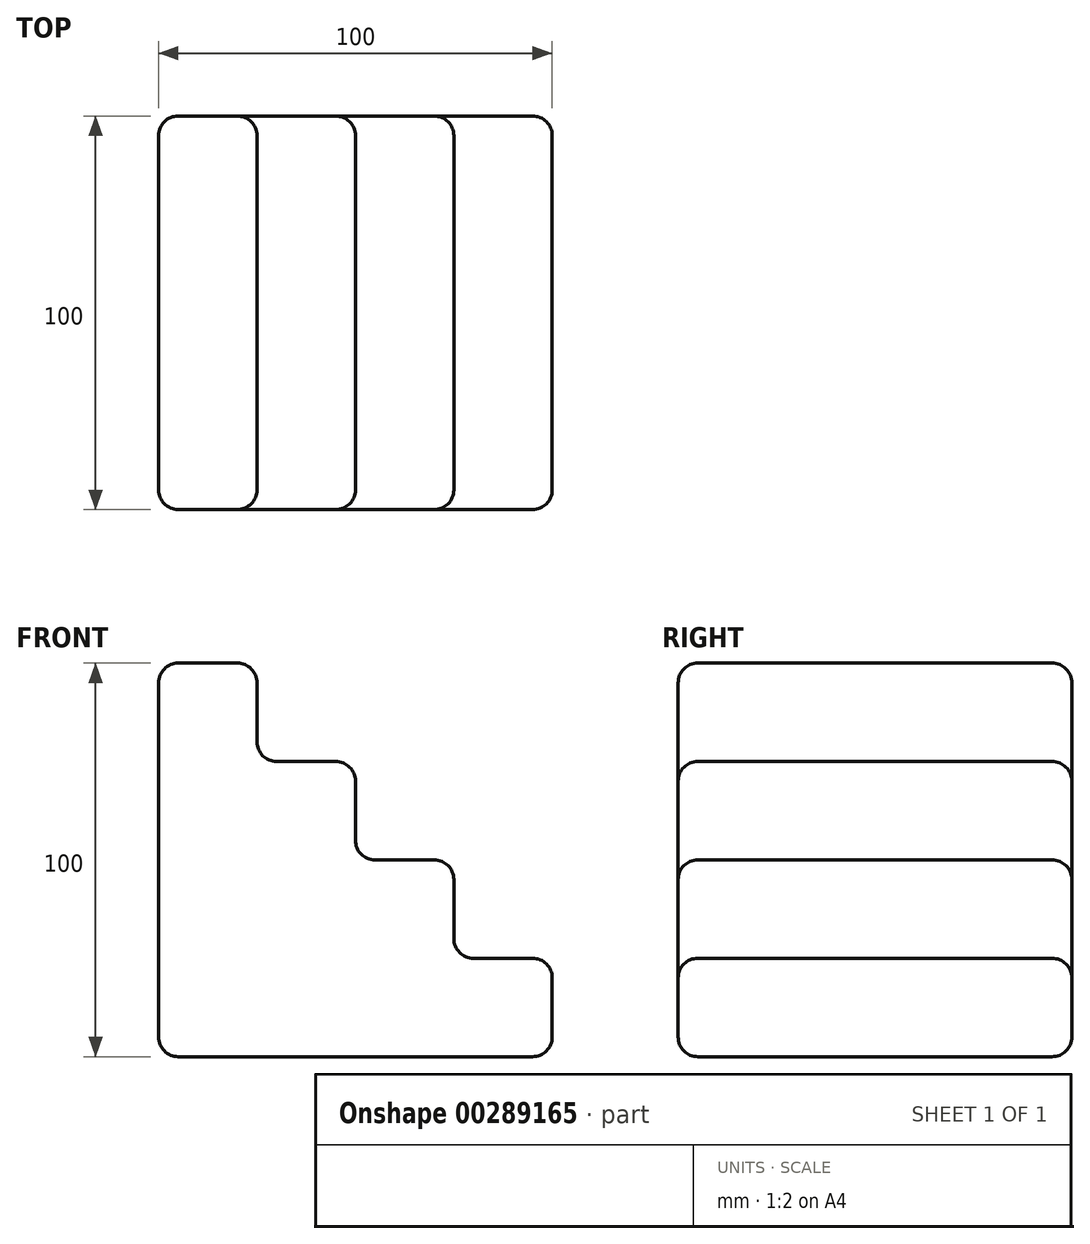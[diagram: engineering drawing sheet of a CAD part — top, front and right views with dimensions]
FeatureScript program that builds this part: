
annotation { "Feature Type Name" : "Feature", "Feature Type Description" : "" }
export const myFeature = defineFeature(function(context is Context, id is Id, definition is map)
    precondition{}
    {
        {
            var Q0;
            Q0=qCreatedBy(makeId("Front.planeOp"),FACE);
            var sketch = newSketch(context, id + "F0", { "sketchPlane" : qUnion([Q0])});
            skLineSegment(sketch, "E0.bottom", {"start": v(0, 0) * mm, "end": v(100, 0) * mm});
            skLineSegment(sketch, "E0.top", {"start": v(0, 100) * mm, "end": v(25, 100) * mm});
            skLineSegment(sketch, "E0.left", {"start": v(0, 0) * mm, "end": v(0, 100) * mm});
            skLineSegment(sketch, "E0.right", {"start": v(100, 0) * mm, "end": v(100, 25) * mm});
            skLineSegment(sketch, "E1", {"start": v(25, 100) * mm, "end": v(25, 75) * mm});
            skLineSegment(sketch, "E2", {"start": v(25, 75) * mm, "end": v(50, 75) * mm});
            skLineSegment(sketch, "E3", {"start": v(50, 75) * mm, "end": v(50, 50) * mm});
            skLineSegment(sketch, "E4", {"start": v(50, 50) * mm, "end": v(75, 50) * mm});
            skLineSegment(sketch, "E5", {"start": v(75, 50) * mm, "end": v(75, 25) * mm});
            skLineSegment(sketch, "E6", {"start": v(75, 25) * mm, "end": v(100, 25) * mm});
            skSolve(sketch);
        }
        {
            var Q0;
            Q0=makeQuery(id+"F0.imprint","IMPRINT",FACE,{"disambiguationData":[TD([[makeQuery(id+"F0.imprint","IMPRINT",EDGE,{"derivedFrom":sQuery(id+"F0.wireOp",EDGE,"E0.bottom")}),1.0]])]});
            extrude(context, id + "F1", {"entities" : qUnion([Q0]), "depth" : 100 * mm});
        }
        {
            var Q0;
            Q0=makeQuery(id+"F1.opExtrude","SWEPT_EDGE",EDGE,{"disambiguationData":[OSD([sQuery(id+"F0.wireOp",EDGE,"E0.top"),sQuery(id+"F0.wireOp",EDGE,"E1")])]});
            var Q1;
            Q1=makeQuery(id+"F1.opExtrude","SWEPT_EDGE",EDGE,{"disambiguationData":[OSD([sQuery(id+"F0.wireOp",EDGE,"E1"),sQuery(id+"F0.wireOp",EDGE,"E2")])]});
            var Q2;
            Q2=makeQuery(id+"F1.opExtrude","SWEPT_EDGE",EDGE,{"disambiguationData":[OSD([sQuery(id+"F0.wireOp",EDGE,"E2"),sQuery(id+"F0.wireOp",EDGE,"E3")])]});
            var Q3;
            Q3=makeQuery(id+"F1.opExtrude","SWEPT_EDGE",EDGE,{"disambiguationData":[OSD([sQuery(id+"F0.wireOp",EDGE,"E3"),sQuery(id+"F0.wireOp",EDGE,"E4")])]});
            var Q4;
            Q4=makeQuery(id+"F1.opExtrude","SWEPT_EDGE",EDGE,{"disambiguationData":[OSD([sQuery(id+"F0.wireOp",EDGE,"E4"),sQuery(id+"F0.wireOp",EDGE,"E5")])]});
            var Q5;
            Q5=makeQuery(id+"F1.opExtrude","SWEPT_EDGE",EDGE,{"disambiguationData":[OSD([sQuery(id+"F0.wireOp",EDGE,"E5"),sQuery(id+"F0.wireOp",EDGE,"E6")])]});
            var Q6;
            Q6=makeQuery(id+"F1.opExtrude","SWEPT_EDGE",EDGE,{"disambiguationData":[OSD([sQuery(id+"F0.wireOp",EDGE,"E0.right"),sQuery(id+"F0.wireOp",EDGE,"E6")])]});
            var Q7;
            Q7=makeQuery(id+"F1.opExtrude","CAP_EDGE",EDGE,{"disambiguationData":[OSD([sQuery(id+"F0.wireOp",EDGE,"E0.right")])],"isStart":false});
            var Q8;
            Q8=makeQuery(id+"F1.opExtrude","SWEPT_EDGE",EDGE,{"disambiguationData":[OSD([sQuery(id+"F0.wireOp",EDGE,"E0.bottom"),sQuery(id+"F0.wireOp",EDGE,"E0.right")])]});
            var Q9;
            Q9=makeQuery(id+"F1.opExtrude","CAP_EDGE",EDGE,{"disambiguationData":[OSD([sQuery(id+"F0.wireOp",EDGE,"E0.right")])],"isStart":true});
            var Q10;
            Q10=makeQuery(id+"F1.opExtrude","CAP_EDGE",EDGE,{"disambiguationData":[OSD([sQuery(id+"F0.wireOp",EDGE,"E6")])],"isStart":false});
            var Q11;
            Q11=makeQuery(id+"F1.opExtrude","CAP_EDGE",EDGE,{"disambiguationData":[OSD([sQuery(id+"F0.wireOp",EDGE,"E5")])],"isStart":false});
            var Q12;
            Q12=makeQuery(id+"F1.opExtrude","SWEPT_FACE",FACE,{"disambiguationData":[OSD([sQuery(id+"F0.wireOp",EDGE,"E4")])]});
            var Q13;
            Q13=makeQuery(id+"F1.opExtrude","CAP_FACE",FACE,{"disambiguationData":[OSD([sQuery(id+"F0.wireOp",EDGE,"E0.bottom"),sQuery(id+"F0.wireOp",EDGE,"E0.top"),sQuery(id+"F0.wireOp",EDGE,"E0.left"),sQuery(id+"F0.wireOp",EDGE,"E0.right"),sQuery(id+"F0.wireOp",EDGE,"E1"),sQuery(id+"F0.wireOp",EDGE,"E2"),sQuery(id+"F0.wireOp",EDGE,"E3"),sQuery(id+"F0.wireOp",EDGE,"E4"),sQuery(id+"F0.wireOp",EDGE,"E5"),sQuery(id+"F0.wireOp",EDGE,"E6")])],"isStart":false});
            var Q14;
            Q14=makeQuery(id+"F1.opExtrude","CAP_FACE",FACE,{"disambiguationData":[OSD([sQuery(id+"F0.wireOp",EDGE,"E0.bottom"),sQuery(id+"F0.wireOp",EDGE,"E0.top"),sQuery(id+"F0.wireOp",EDGE,"E0.left"),sQuery(id+"F0.wireOp",EDGE,"E0.right"),sQuery(id+"F0.wireOp",EDGE,"E1"),sQuery(id+"F0.wireOp",EDGE,"E2"),sQuery(id+"F0.wireOp",EDGE,"E3"),sQuery(id+"F0.wireOp",EDGE,"E4"),sQuery(id+"F0.wireOp",EDGE,"E5"),sQuery(id+"F0.wireOp",EDGE,"E6")])],"isStart":true});
            var Q15;
            Q15=makeQuery(id+"F1.opExtrude","SWEPT_FACE",FACE,{"disambiguationData":[OSD([sQuery(id+"F0.wireOp",EDGE,"E0.left")])]});
            fillet(context, id + "F2", {"entities" : qUnion([Q0, Q1, Q2, Q3, Q4, Q5, Q6, Q7, Q8, Q9, Q10, Q11, Q12, Q13, Q14, Q15]), "radius" : 5 * mm, "tangentPropagation" : true, "allowEdgeOverflow" : false});
        }
    });
